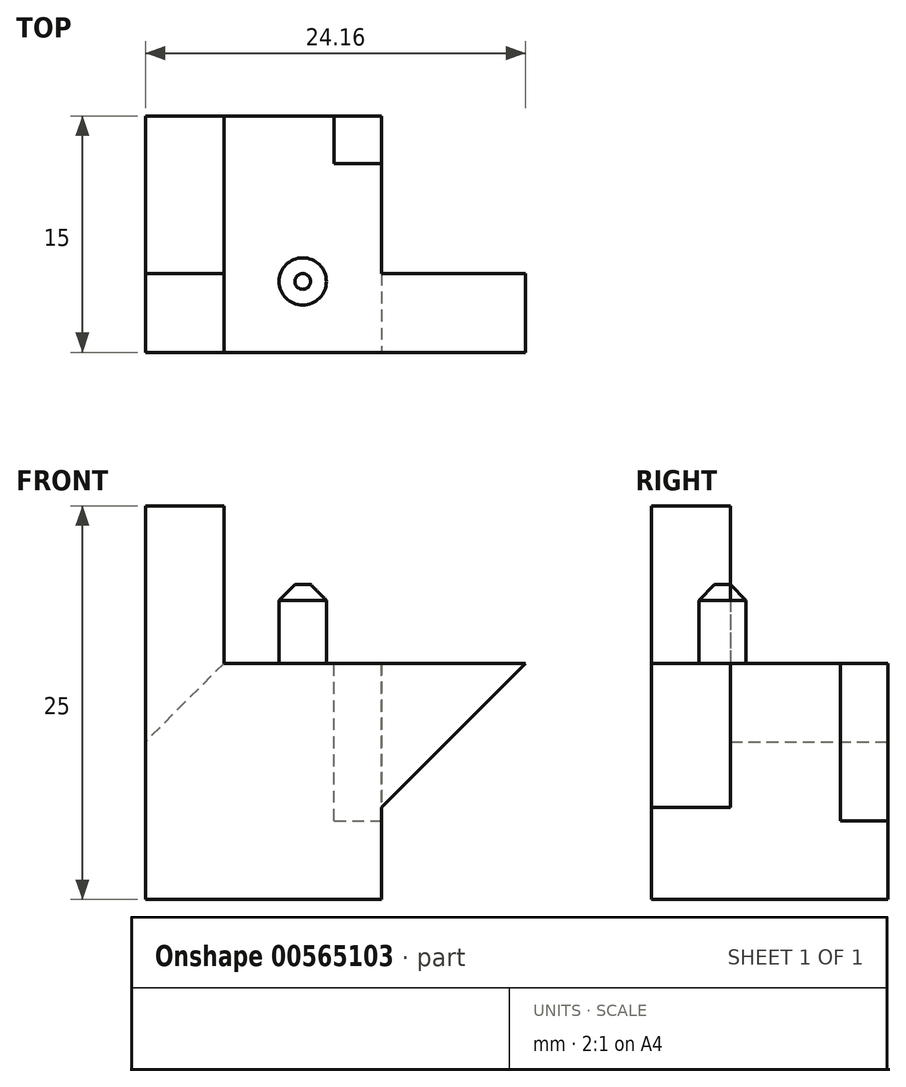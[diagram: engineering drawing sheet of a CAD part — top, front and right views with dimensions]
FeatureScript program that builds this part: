
annotation { "Feature Type Name" : "Feature", "Feature Type Description" : "" }
export const myFeature = defineFeature(function(context is Context, id is Id, definition is map)
    precondition{}
    {
        {
            var Q0;
            Q0=qCreatedBy(makeId("Top.planeOp"),FACE);
            var sketch = newSketch(context, id + "F0", { "sketchPlane" : qUnion([Q0])});
            skLineSegment(sketch, "E0.bottom", {"start": v(0, -7.5) * mm, "end": v(15, -7.5) * mm});
            skLineSegment(sketch, "E0.top", {"start": v(0, 7.5) * mm, "end": v(15, 7.5) * mm});
            skLineSegment(sketch, "E0.left", {"start": v(0, -7.5) * mm, "end": v(0, 7.5) * mm});
            skLineSegment(sketch, "E0.right", {"start": v(15, -7.5) * mm, "end": v(15, 7.5) * mm});
            skSolve(sketch);
        }
        {
            var Q0;
            Q0=makeQuery(id+"F0.imprint","IMPRINT",FACE,{"disambiguationData":[TD([[makeQuery(id+"F0.imprint","IMPRINT",EDGE,{"derivedFrom":sQuery(id+"F0.wireOp",EDGE,"E0.bottom")}),1.0]])]});
            extrude(context, id + "F1", {"entities" : qUnion([Q0]), "depth" : 15 * mm, "offsetDistance" : 25 * mm});
        }
        {
            var Q0;
            Q0=makeQuery(id+"F1.opExtrude","CAP_FACE",FACE,{"disambiguationData":[OSD([sQuery(id+"F0.wireOp",EDGE,"E0.bottom"),sQuery(id+"F0.wireOp",EDGE,"E0.top"),sQuery(id+"F0.wireOp",EDGE,"E0.left"),sQuery(id+"F0.wireOp",EDGE,"E0.right")])],"isStart":false});
            var sketch = newSketch(context, id + "F2", { "sketchPlane" : qUnion([Q0])});
            skCircle(sketch, "E1", {"center": v(10, -3) * mm, "radius": 1.5 * mm});
            skLineSegment(sketch, "E2.bottom", {"start": v(15, 7.5) * mm, "end": v(12, 7.5) * mm});
            skLineSegment(sketch, "E2.top", {"start": v(15, 4.5) * mm, "end": v(12, 4.5) * mm});
            skLineSegment(sketch, "E2.left", {"start": v(15, 7.5) * mm, "end": v(15, 4.5) * mm});
            skLineSegment(sketch, "E2.right", {"start": v(12, 7.5) * mm, "end": v(12, 4.5) * mm});
            skLineSegment(sketch, "E3.bottom", {"start": v(0, -7.5) * mm, "end": v(5, -7.5) * mm});
            skLineSegment(sketch, "E3.top", {"start": v(0, -2.5) * mm, "end": v(5, -2.5) * mm});
            skLineSegment(sketch, "E3.left", {"start": v(0, -7.5) * mm, "end": v(0, -2.5) * mm});
            skLineSegment(sketch, "E3.right", {"start": v(5, -7.5) * mm, "end": v(5, -2.5) * mm});
            skSolve(sketch);
        }
        {
            var Q0;
            Q0=makeQuery(id+"F2.imprint","IMPRINT",FACE,{"disambiguationData":[TD([[makeQuery(id+"F2.imprint","IMPRINT",EDGE,{"derivedFrom":sQuery(id+"F2.wireOp",EDGE,"E3.bottom")}),1.0]])]});
            extrude(context, id + "F3", {"entities" : qUnion([Q0]), "operationType" : NewBodyOperationType.ADD, "depth" : 10 * mm, "offsetDistance" : 25 * mm});
        }
        {
            var Q0;
            Q0=makeQuery(id+"F2.imprint","IMPRINT",FACE,{"disambiguationData":[TD([[makeQuery(id+"F2.imprint","IMPRINT",EDGE,{"derivedFrom":sQuery(id+"F2.wireOp",EDGE,"E1")}),1.0]])]});
            extrude(context, id + "F4", {"entities" : qUnion([Q0]), "operationType" : NewBodyOperationType.ADD, "depth" : 5 * mm, "offsetDistance" : 25 * mm});
        }
        {
            var Q0;
            Q0=makeQuery(id+"F2.imprint","IMPRINT",FACE,{"disambiguationData":[TD([[makeQuery(id+"F2.imprint","IMPRINT",EDGE,{"derivedFrom":sQuery(id+"F2.wireOp",EDGE,"E2.bottom")}),-1.0]])]});
            extrude(context, id + "F5", {"entities" : qUnion([Q0]), "operationType" : NewBodyOperationType.REMOVE, "oppositeDirection" : true, "depth" : 10 * mm, "offsetDistance" : 25 * mm});
        }
        {
            var Q0;
            Q0=makeQuery(id+"F1.opExtrude","CAP_EDGE",EDGE,{"disambiguationData":[OSD([sQuery(id+"F0.wireOp",EDGE,"E0.left")])],"isStart":false});
            chamfer(context, id + "F6", {"entities" : qUnion([Q0]), "width" : 5 * mm, "tangentPropagation" : true});
        }
        {
            var Q0;
            Q0=makeQuery(id+"F3.boolean.opBoolean","MERGE",FACE,{"derivedFrom":[makeQuery(id+"F1.opExtrude","SWEPT_FACE",FACE,{"disambiguationData":[OSD([sQuery(id+"F0.wireOp",EDGE,"E0.bottom")])]}),makeQuery(id+"F3.opExtrude","SWEPT_FACE",FACE,{"disambiguationData":[OSD([sQuery(id+"F2.wireOp",EDGE,"E3.bottom")])]})]});
            var sketch = newSketch(context, id + "F7", { "sketchPlane" : qUnion([Q0])});
            skLineSegment(sketch, "E4", {"start": v(15, 15) * mm, "end": v(24.16, 15) * mm});
            skLineSegment(sketch, "E5", {"start": v(15, 5.84) * mm, "end": v(24.16, 15) * mm});
            skLineSegment(sketch, "E6", {"start": v(15, 5.84) * mm, "end": v(15, 15) * mm});
            skSolve(sketch);
        }
        {
            var Q0;
            Q0=makeQuery(id+"F7.imprint","IMPRINT",FACE,{"disambiguationData":[TD([[makeQuery(id+"F7.imprint","IMPRINT",EDGE,{"derivedFrom":sQuery(id+"F7.wireOp",EDGE,"E4")}),-1.0]])]});
            extrude(context, id + "F8", {"entities" : qUnion([Q0]), "operationType" : NewBodyOperationType.ADD, "oppositeDirection" : true, "depth" : 5 * mm, "offsetDistance" : 25 * mm});
        }
        {
            var Q0;
            Q0=makeQuery(id+"F4.opExtrude","CAP_EDGE",EDGE,{"disambiguationData":[OSD([sQuery(id+"F2.wireOp",EDGE,"E1")])],"isStart":false});
            chamfer(context, id + "F9", {"entities" : qUnion([Q0]), "width" : 1 * mm, "tangentPropagation" : true});
        }
    });
